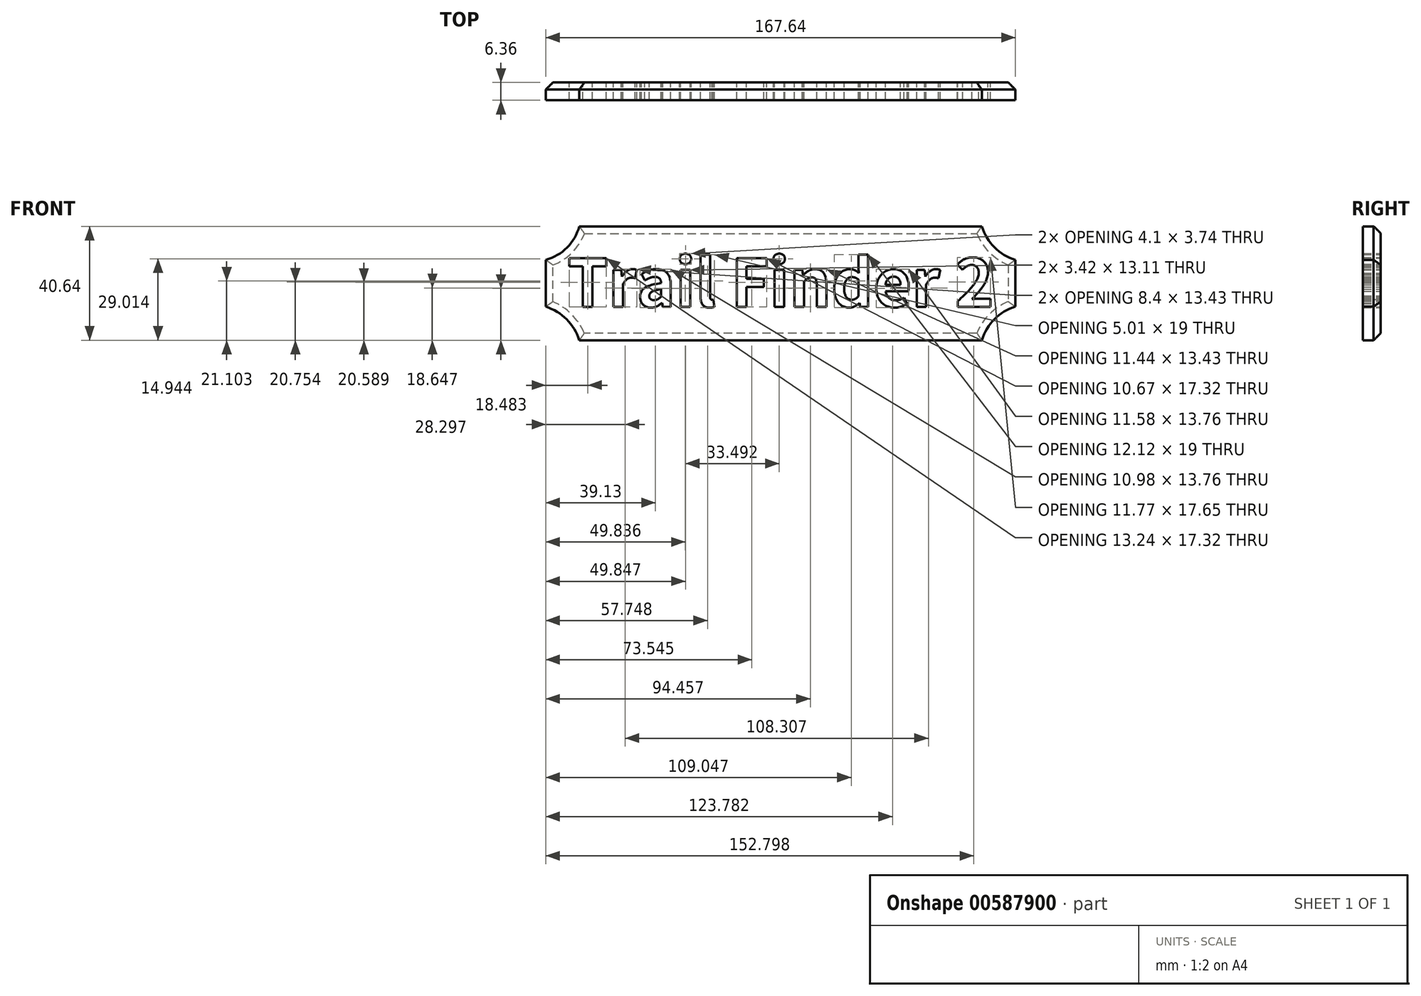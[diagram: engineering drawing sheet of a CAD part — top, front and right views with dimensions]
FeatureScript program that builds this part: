
annotation { "Feature Type Name" : "Feature", "Feature Type Description" : "" }
export const myFeature = defineFeature(function(context is Context, id is Id, definition is map)
    precondition{}
    {
        {
            var Q0;
            Q0=qCreatedBy(makeId("Front.planeOp"),FACE);
            var sketch = newSketch(context, id + "F0", { "sketchPlane" : qUnion([Q0])});
            skLineSegment(sketch, "E0", {"start": v(-71.87, 20.33) * mm, "end": v(71.86, 20.33) * mm});
            skLineSegment(sketch, "E1", {"start": v(-71.87, -20.3) * mm, "end": v(71.86, -20.3) * mm});
            skLineSegment(sketch, "E2", {"start": v(-83.82, 8.37) * mm, "end": v(-83.82, -8.35) * mm});
            skLineSegment(sketch, "E3", {"start": v(83.82, 8.37) * mm, "end": v(83.82, -8.35) * mm});
            skArc(sketch, "E4", {"start": v(-83.82, 8.37) * mm, "mid": v(-76.24, 12.75) * mm, "end": v(-71.87, 20.33) * mm});
            skArc(sketch, "E5", {"start": v(-71.87, -20.3) * mm, "mid": v(-76.39, -12.87) * mm, "end": v(-83.82, -8.35) * mm});
            skArc(sketch, "E6", {"start": v(71.86, 20.33) * mm, "mid": v(76.34, 12.85) * mm, "end": v(83.82, 8.37) * mm});
            skArc(sketch, "E7", {"start": v(83.82, -8.35) * mm, "mid": v(76.33, -12.83) * mm, "end": v(71.86, -20.3) * mm});
            skSolve(sketch);
        }
        {
            var Q0;
            Q0=qCreatedBy(makeId("Front.planeOp"),FACE);
            var sketch = newSketch(context, id + "F1", { "sketchPlane" : qUnion([Q0])});
            skText(sketch, "E8", { "text": "Trail Finder 2", "fontName": "NotoSansCJKkr-Bold.otf"});
            const initialGuessF1  = {"E8": [-0.0762, -0.00838, 1, 0, 0.01685]};
            skSetInitialGuess(sketch, initialGuessF1);
            skSolve(sketch);
        }
        {
            var Q0;
            Q0=makeQuery(id+"F0.imprint","IMPRINT",FACE,{"disambiguationData":[TD([[makeQuery(id+"F0.imprint","IMPRINT",EDGE,{"derivedFrom":sQuery(id+"F0.wireOp",EDGE,"E0")}),-1.0]])]});
            extrude(context, id + "F2", {"entities" : qUnion([Q0]), "endBound" : BoundingType.SYMMETRIC, "depth" : 6.35 * mm, "offsetDistance" : 25.4 * mm});
        }
        {
            var Q0;
            Q0 = qSketchRegion(id + "F1", true);
            extrude(context, id + "F3", {"entities" : qUnion([Q0]), "operationType" : NewBodyOperationType.REMOVE, "endBound" : BoundingType.SYMMETRIC, "depth" : 12.7 * mm, "offsetDistance" : 25.4 * mm});
        }
        {
            var Q0;
            Q0=makeQuery(id+"F2.opExtrude","CAP_EDGE",EDGE,{"disambiguationData":[OSD([sQuery(id+"F0.wireOp",EDGE,"E0")])],"isStart":true});
            var Q1;
            Q1=makeQuery(id+"F2.opExtrude","CAP_EDGE",EDGE,{"disambiguationData":[OSD([sQuery(id+"F0.wireOp",EDGE,"E2")])],"isStart":true});
            var Q2;
            Q2=makeQuery(id+"F2.opExtrude","CAP_EDGE",EDGE,{"disambiguationData":[OSD([sQuery(id+"F0.wireOp",EDGE,"E4")])],"isStart":true});
            var Q3;
            Q3=makeQuery(id+"F2.opExtrude","CAP_EDGE",EDGE,{"disambiguationData":[OSD([sQuery(id+"F0.wireOp",EDGE,"E6")])],"isStart":true});
            var Q4;
            Q4=makeQuery(id+"F2.opExtrude","CAP_EDGE",EDGE,{"disambiguationData":[OSD([sQuery(id+"F0.wireOp",EDGE,"E3")])],"isStart":true});
            var Q5;
            Q5=makeQuery(id+"F2.opExtrude","CAP_EDGE",EDGE,{"disambiguationData":[OSD([sQuery(id+"F0.wireOp",EDGE,"E7")])],"isStart":true});
            var Q6;
            Q6=makeQuery(id+"F2.opExtrude","CAP_EDGE",EDGE,{"disambiguationData":[OSD([sQuery(id+"F0.wireOp",EDGE,"E1")])],"isStart":true});
            var Q7;
            Q7=makeQuery(id+"F2.opExtrude","CAP_EDGE",EDGE,{"disambiguationData":[OSD([sQuery(id+"F0.wireOp",EDGE,"E5")])],"isStart":true});
            chamfer(context, id + "F4", {"entities" : qUnion([Q0, Q1, Q2, Q3, Q4, Q5, Q6, Q7]), "width" : 2.54 * mm, "tangentPropagation" : true});
        }
    });
